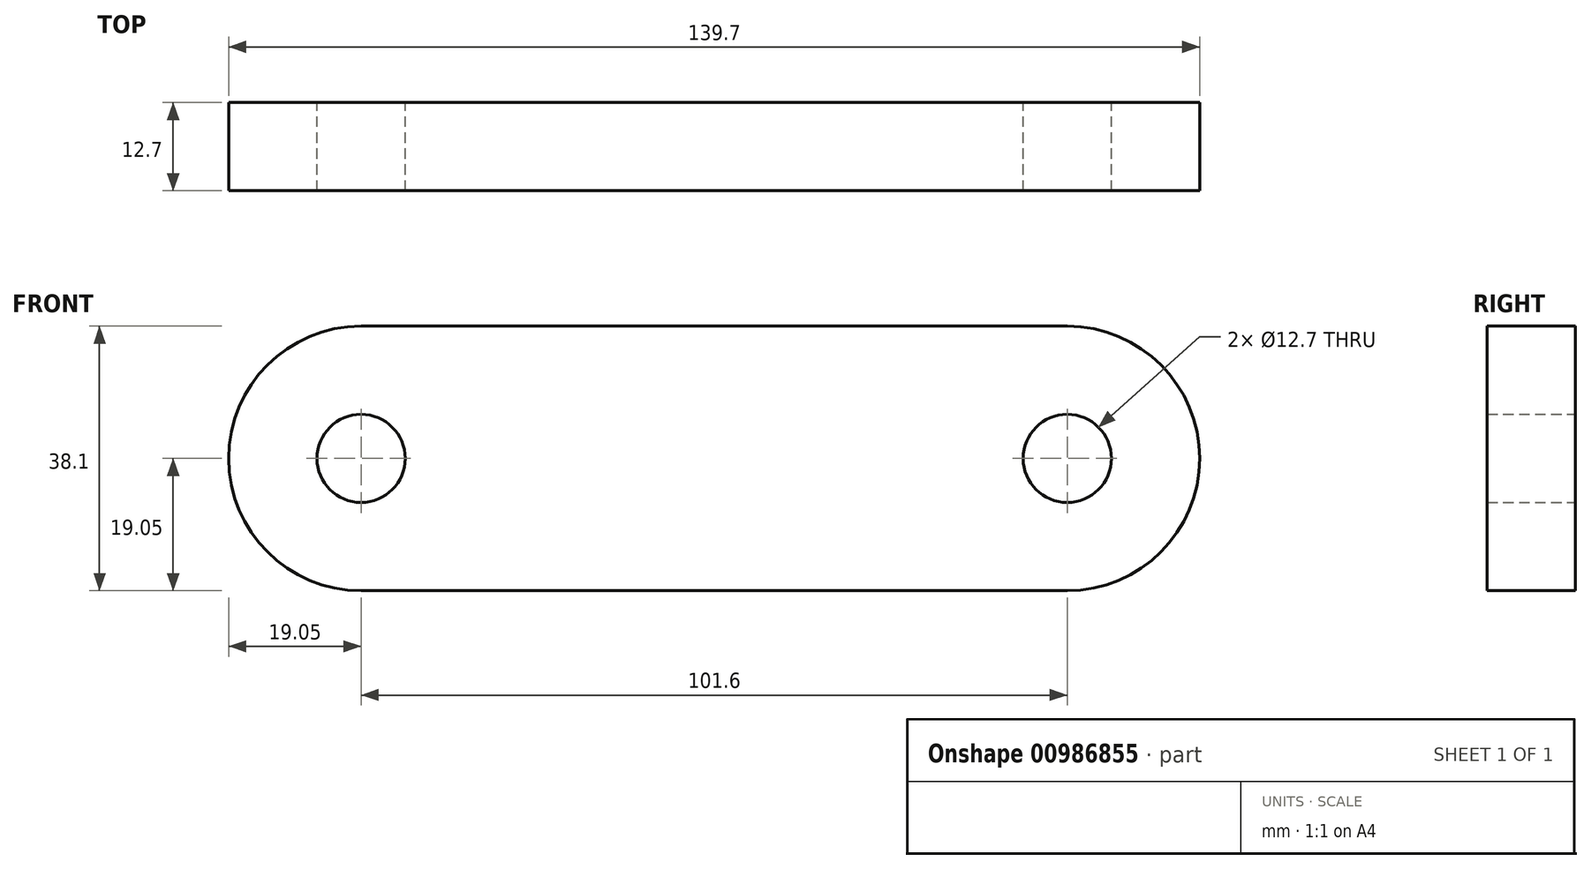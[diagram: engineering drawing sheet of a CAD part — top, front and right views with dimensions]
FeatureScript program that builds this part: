
annotation { "Feature Type Name" : "Feature", "Feature Type Description" : "" }
export const myFeature = defineFeature(function(context is Context, id is Id, definition is map)
    precondition{}
    {
        {
            var Q0;
            Q0=qCreatedBy(makeId("Front.planeOp"),FACE);
            var sketch = newSketch(context, id + "F0", { "sketchPlane" : qUnion([Q0])});
            skCircle(sketch, "E0", {"center": v(0, 0) * mm, "radius": 6.35 * mm});
            skCircle(sketch, "E1", {"center": v(101.6, 0) * mm, "radius": 6.35 * mm});
            skArc(sketch, "E2", {"start": v(0, 19.05) * mm, "mid": v(-19.05, 0) * mm, "end": v(0, -19.05) * mm});
            skArc(sketch, "E3", {"start": v(101.6, -19.05) * mm, "mid": v(120.65, 0) * mm, "end": v(101.6, 19.05) * mm});
            skLineSegment(sketch, "E4", {"start": v(0, 19.05) * mm, "end": v(101.6, 19.05) * mm});
            skLineSegment(sketch, "E5", {"start": v(0, -19.05) * mm, "end": v(101.6, -19.05) * mm});
            skSolve(sketch);
        }
        {
            var Q0;
            Q0 = qSketchRegion(id + "F0", true);
            extrude(context, id + "F1", {"entities" : qUnion([Q0]), "endBound" : BoundingType.SYMMETRIC, "depth" : 12.7 * mm, "offsetDistance" : 25.4 * mm});
        }
    });
